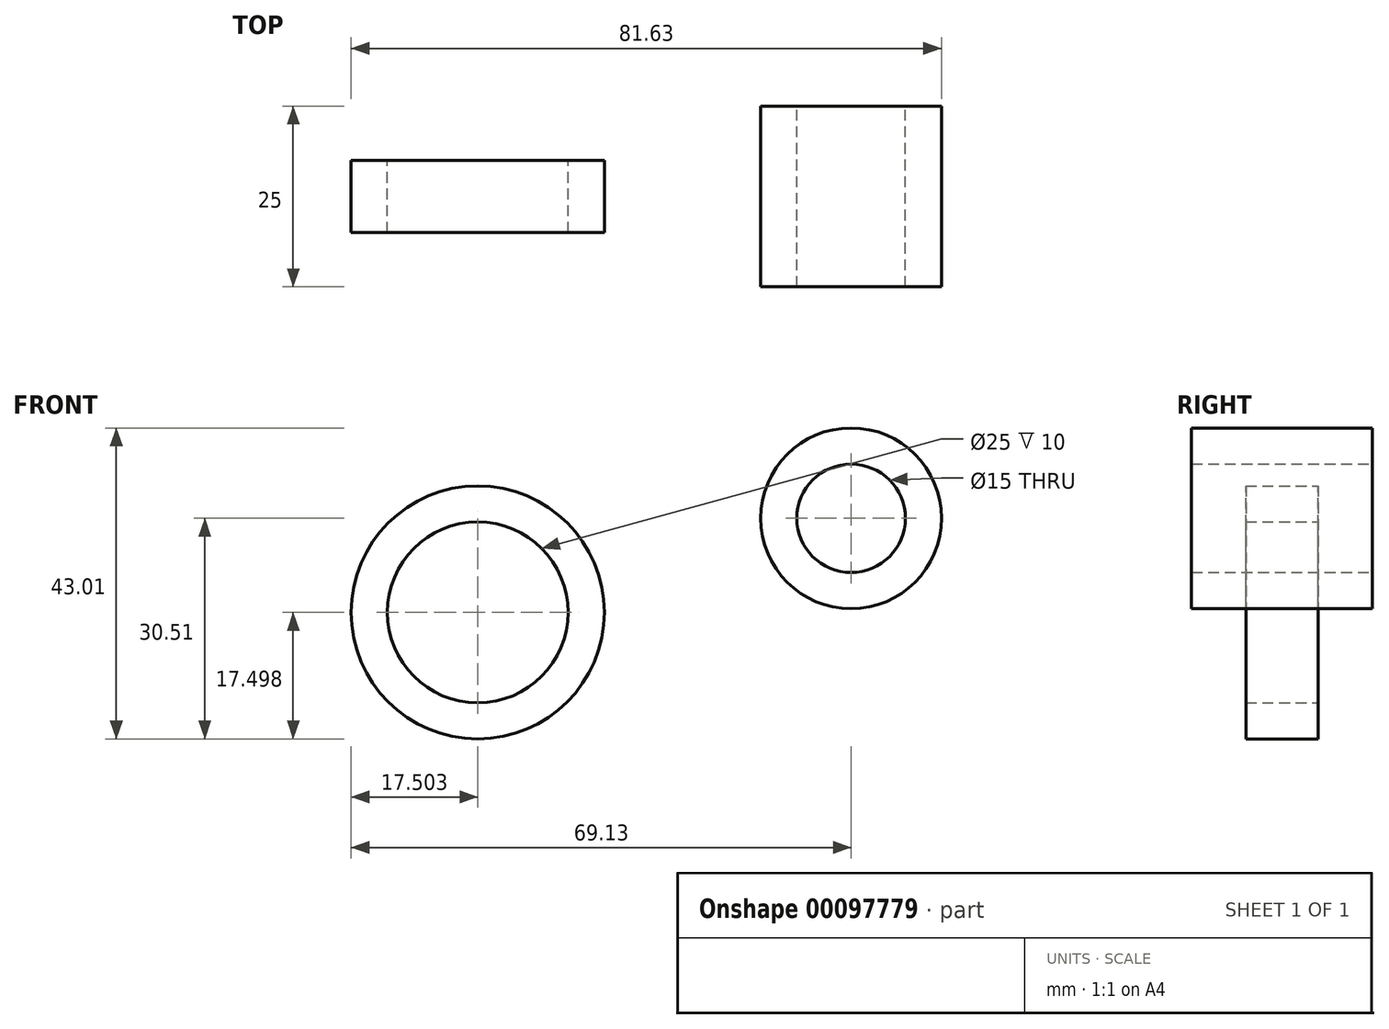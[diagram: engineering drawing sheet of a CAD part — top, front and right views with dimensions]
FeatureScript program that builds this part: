
annotation { "Feature Type Name" : "Feature", "Feature Type Description" : "" }
export const myFeature = defineFeature(function(context is Context, id is Id, definition is map)
    precondition{}
    {
        {
            var Q0;
            Q0=qCreatedBy(makeId("Front.planeOp"),FACE);
            var sketch = newSketch(context, id + "F0", { "sketchPlane" : qUnion([Q0])});
            skCircle(sketch, "E0", {"center": v(0, 0) * mm, "radius": 7.5 * mm});
            skCircle(sketch, "E1", {"center": v(0, 0) * mm, "radius": 12.5 * mm});
            skSolve(sketch);
        }
        {
            var Q0;
            Q0=makeQuery(id+"F0.imprint","IMPRINT",FACE,{"disambiguationData":[TD([[makeQuery(id+"F0.imprint","IMPRINT",EDGE,{"derivedFrom":sQuery(id+"F0.wireOp",EDGE,"E0")}),-1.0]])]});
            extrude(context, id + "F1", {"entities" : qUnion([Q0]), "endBound" : BoundingType.SYMMETRIC, "depth" : 25 * mm});
        }
        {
            var Q0;
            Q0=qCreatedBy(makeId("Front.planeOp"),FACE);
            var sketch = newSketch(context, id + "F2", { "sketchPlane" : qUnion([Q0])});
            skCircle(sketch, "E2", {"center": v(-51.63, -13.01) * mm, "radius": 12.5 * mm});
            skCircle(sketch, "E3", {"center": v(-51.63, -13.01) * mm, "radius": 17.5 * mm});
            skSolve(sketch);
        }
        {
            var Q0;
            Q0=makeQuery(id+"F2.imprint","IMPRINT",FACE,{"disambiguationData":[TD([[makeQuery(id+"F2.imprint","IMPRINT",EDGE,{"derivedFrom":sQuery(id+"F2.wireOp",EDGE,"E2")}),-1.0]])]});
            extrude(context, id + "F3", {"entities" : qUnion([Q0]), "endBound" : BoundingType.SYMMETRIC, "depth" : 10 * mm});
        }
    });
